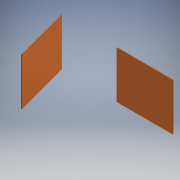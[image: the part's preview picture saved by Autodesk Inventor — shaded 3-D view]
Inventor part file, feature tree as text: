
AUTODESK INVENTOR PART (.ipt)
format: ipt  version: 2016 (Build 200138000, 138)  size: 166,400 bytes
history: native  units: mm
features: extrude x3, sketch x3, projected_geometry x1
ambient origin geometry x8: Origin, YZ Plane, XZ Plane, XY Plane, X Axis, Y Axis, Z Axis, Center Point
bodies: Solid1 (feature_tree)
feature tree (7):
  extrude  "Extrusion1"  Depth=50.0mm
  extrude  "Extrusión10"  Depth=6.0mm
  extrude  "Extrusión11"  TaperAngle=0.0deg  [1 undecoded]
  sketch  "Sketch1"  dims[d2=41.0mm d3=50.0mm]
  sketch  "Boceto10"  dims[d4=100.0mm d5=6.0mm]
  sketch  "Boceto11"  dims[d6=6.0mm d8=0.0mm d49=848.75mm d50=848.75mm d52=10.0mm d53=848.75mm d54=820.0mm d55=0.0mm d56=41.0mm d57=50.0mm d58=100.0mm d59=6.0mm d60=6.0mm d61=820.0mm d62=0.0mm]
  projected_geometry  "Contorno proyectado8"
note: 1 required parameter value undecoded (feature->parameter linkage not recoverable at this tier; creation-order binding heuristic only, values carry confidence <= 0.55)
